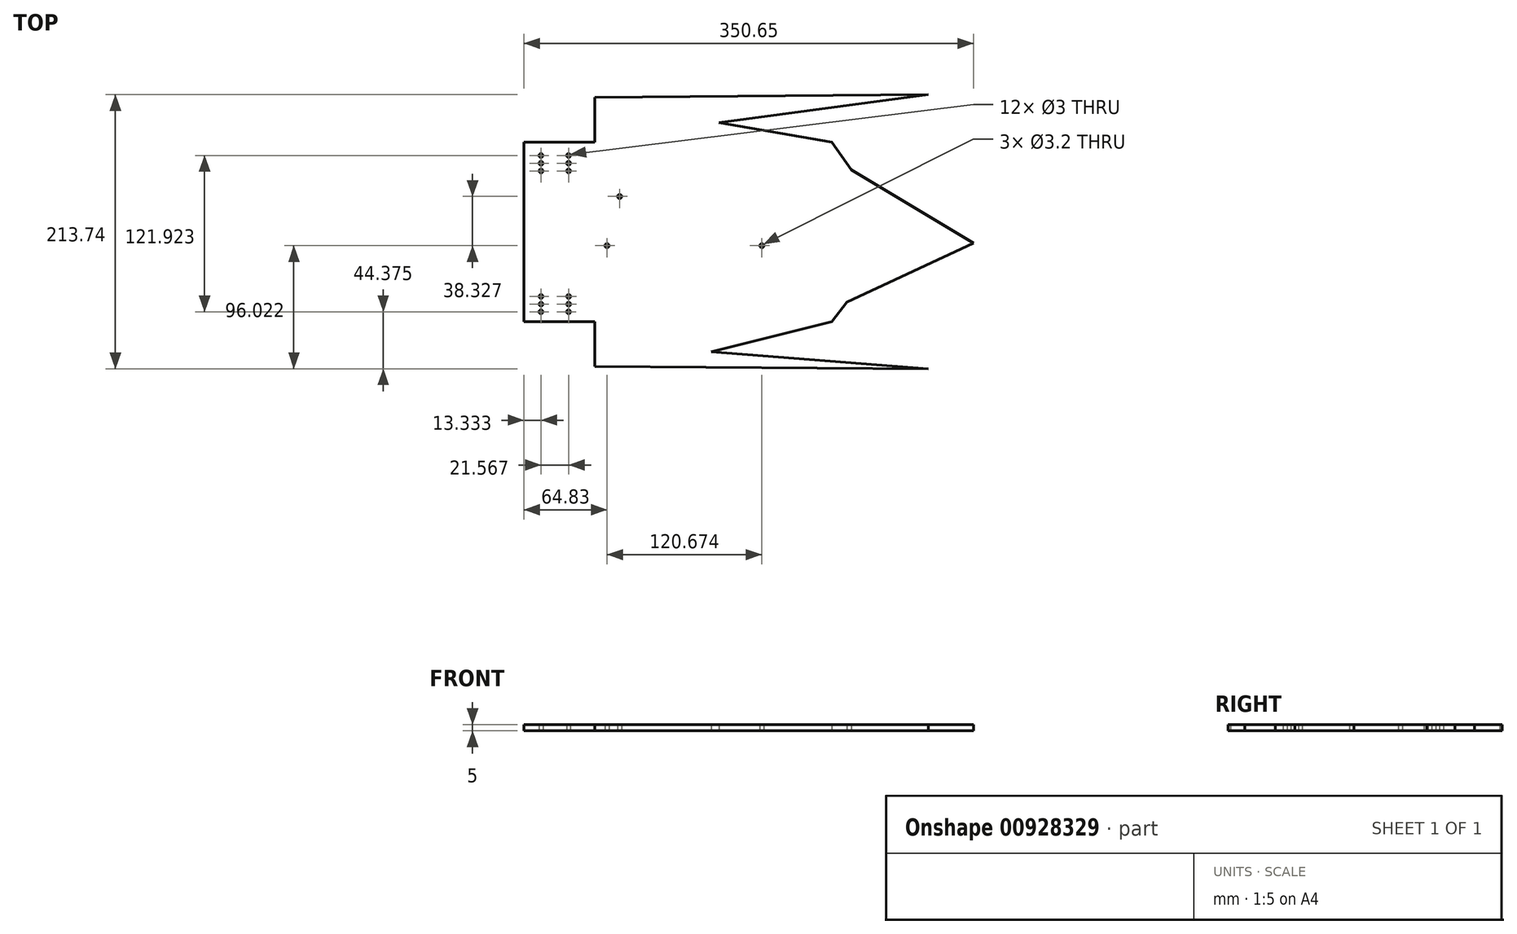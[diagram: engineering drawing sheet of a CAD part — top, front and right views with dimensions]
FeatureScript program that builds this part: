
annotation { "Feature Type Name" : "Feature", "Feature Type Description" : "" }
export const myFeature = defineFeature(function(context is Context, id is Id, definition is map)
    precondition{}
    {
        {
            var Q0;
            Q0=qCreatedBy(makeId("Top.planeOp"),FACE);
            var sketch = newSketch(context, id + "F0", { "sketchPlane" : qUnion([Q0])});
            skLineSegment(sketch, "E0.bottom", {"start": v(-128.56, -28.37) * mm, "end": v(111.44, -28.37) * mm});
            skLineSegment(sketch, "E0.top", {"start": v(-128.56, -168.37) * mm, "end": v(111.44, -168.37) * mm});
            skLineSegment(sketch, "E0.left", {"start": v(-128.56, -28.37) * mm, "end": v(-128.56, -168.37) * mm});
            skLineSegment(sketch, "E0.right", {"start": v(111.44, -28.37) * mm, "end": v(111.44, -168.37) * mm});
            skCircle(sketch, "E1", {"center": v(-115.23, -38.77) * mm, "radius": 1.5 * mm});
            skPoint(sketch, "E2.start.orphan", {"position": v(-73.23, -28.37) * mm});
            skPoint(sketch, "E3.start.orphan", {"position": v(-73.23, -168.37) * mm});
            skLineSegment(sketch, "E4", {"start": v(111.44, -28.37) * mm, "end": v(23.59, -12.98) * mm});
            skPoint(sketch, "E5.end.orphan", {"position": v(186.77, -205.07) * mm});
            skPoint(sketch, "E6", {"position": v(17.53, -28.37) * mm});
            skPoint(sketch, "E7.end.orphan", {"position": v(17.53, -191.94) * mm});
            skLineSegment(sketch, "E8", {"start": v(-73.23, -203.37) * mm, "end": v(186.77, -205.07) * mm});
            skLineSegment(sketch, "E9", {"start": v(186.77, -205.07) * mm, "end": v(17.53, -191.94) * mm});
            skPoint(sketch, "E10.start.orphan", {"position": v(186.77, 110.3) * mm});
            skLineSegment(sketch, "E11", {"start": v(186.77, 8.67) * mm, "end": v(23.59, -12.98) * mm});
            skLineSegment(sketch, "E12", {"start": v(-73.23, 6.63) * mm, "end": v(186.77, 8.67) * mm});
            skLineSegment(sketch, "E13", {"start": v(17.53, -191.94) * mm, "end": v(111.44, -168.37) * mm});
            skPoint(sketch, "E14", {"position": v(111.44, -98.37) * mm});
            skLineSegment(sketch, "E15", {"start": v(111.44, -28.37) * mm, "end": v(163.17, -102.02) * mm});
            skLineSegment(sketch, "E16", {"start": v(163.17, -102.02) * mm, "end": v(111.44, -168.37) * mm});
            skLineSegment(sketch, "E17", {"start": v(123.3, -153.15) * mm, "end": v(222.1, -107) * mm});
            skLineSegment(sketch, "E18", {"start": v(222.1, -107) * mm, "end": v(126.68, -50.07) * mm});
            skPoint(sketch, "E19.orphan", {"position": v(-73.23, -38.77) * mm});
            skPoint(sketch, "E20.end.orphan", {"position": v(-73.23, 89.23) * mm});
            skCircle(sketch, "E21.0.1.0", {"center": v(-115.2, -44.77) * mm, "radius": 1.5 * mm});
            skCircle(sketch, "E21.0.2.0", {"center": v(-115.16, -50.77) * mm, "radius": 1.5 * mm});
            skCircle(sketch, "E21.1.0.0", {"center": v(-93.73, -38.77) * mm, "radius": 1.5 * mm});
            skCircle(sketch, "E21.1.1.0", {"center": v(-93.7, -44.77) * mm, "radius": 1.5 * mm});
            skCircle(sketch, "E21.1.2.0", {"center": v(-93.66, -50.77) * mm, "radius": 1.5 * mm});
            skLineSegment(sketch, "E21.direction1", {"start": v(-115.23, -38.77) * mm, "end": v(-93.73, -38.77) * mm, "construction": true});
            skLineSegment(sketch, "E21.direction2", {"start": v(-115.23, -38.77) * mm, "end": v(-115.2, -44.77) * mm, "construction": true});
            skLineSegment(sketch, "E22", {"start": v(-145.17, -99.73) * mm, "end": v(-79.3, -99.73) * mm});
            skCircle(sketch, "E23.MirrorC", {"center": v(-115.23, -160.7) * mm, "radius": 1.5 * mm});
            skCircle(sketch, "E24.MirrorC", {"center": v(-115.2, -154.7) * mm, "radius": 1.5 * mm});
            skCircle(sketch, "E25.MirrorC", {"center": v(-93.73, -160.7) * mm, "radius": 1.5 * mm});
            skCircle(sketch, "E26.MirrorC", {"center": v(-93.66, -148.7) * mm, "radius": 1.5 * mm});
            skCircle(sketch, "E27.MirrorC", {"center": v(-93.7, -154.7) * mm, "radius": 1.5 * mm});
            skCircle(sketch, "E28.MirrorC", {"center": v(-115.16, -148.7) * mm, "radius": 1.5 * mm});
            skLineSegment(sketch, "E29.MirrorCS", {"start": v(-115.23, -160.7) * mm, "end": v(-93.73, -160.7) * mm, "construction": true});
            skLineSegment(sketch, "E30.MirrorCS", {"start": v(-115.23, -160.7) * mm, "end": v(-115.2, -154.7) * mm, "construction": true});
            skLineSegment(sketch, "E31", {"start": v(-73.23, -203.37) * mm, "end": v(-73.23, -168.37) * mm});
            skLineSegment(sketch, "E32", {"start": v(-73.23, -28.37) * mm, "end": v(-73.23, 6.63) * mm});
            skCircle(sketch, "E33", {"center": v(-63.73, -109.05) * mm, "radius": 1.6 * mm});
            skCircle(sketch, "E34", {"center": v(56.94, -109.05) * mm, "radius": 1.6 * mm});
            skLineSegment(sketch, "E35", {"start": v(127.31, 248.47) * mm, "end": v(143.1, 236.19) * mm});
            skCircle(sketch, "E36", {"center": v(16.52, 236.19) * mm, "radius": 1.6 * mm});
            skCircle(sketch, "E37", {"center": v(139.1, 236.19) * mm, "radius": 1.6 * mm});
            skCircle(sketch, "E38", {"center": v(-53.91, -70.72) * mm, "radius": 1.6 * mm});
            skPoint(sketch, "E39.end.orphan", {"position": v(127.31, 223.9) * mm});
            skPoint(sketch, "E40.end.orphan", {"position": v(125.96, 193.94) * mm});
            skCircle(sketch, "E41", {"center": v(7.57, 160.35) * mm, "radius": 15 * mm});
            skLineSegment(sketch, "E42", {"start": v(-58.33, 202.6) * mm, "end": v(-42.54, 214.87) * mm});
            skLineSegment(sketch, "E43", {"start": v(-42.54, 214.87) * mm, "end": v(56.46, 214.87) * mm});
            skLineSegment(sketch, "E44", {"start": v(56.46, 214.87) * mm, "end": v(72.25, 202.6) * mm});
            skLineSegment(sketch, "E45", {"start": v(72.25, 202.6) * mm, "end": v(56.46, 190.32) * mm});
            skLineSegment(sketch, "E46", {"start": v(56.46, 190.32) * mm, "end": v(-42.54, 190.32) * mm});
            skLineSegment(sketch, "E47", {"start": v(-42.54, 190.32) * mm, "end": v(-58.33, 202.6) * mm});
            skLineSegment(sketch, "E48", {"start": v(-42.54, 214.87) * mm, "end": v(-42.54, 190.32) * mm});
            skLineSegment(sketch, "E49", {"start": v(56.46, 214.87) * mm, "end": v(56.46, 190.32) * mm});
            skCircle(sketch, "E50", {"center": v(-54.33, 202.6) * mm, "radius": 1.6 * mm});
            skCircle(sketch, "E51", {"center": v(68.25, 202.6) * mm, "radius": 1.6 * mm});
            skLineSegment(sketch, "E52", {"start": v(7.57, 160.35) * mm, "end": v(55.11, 160.35) * mm});
            skSolve(sketch);
        }
        {
            var Q0;
            {var subQ0=sQuery(id+"F0.wireOp",EDGE,"E0.right");Q0=makeQuery(id+"F0.imprint","IMPRINT",FACE,{"disambiguationData":[TD([[makeQuery(id+"F0.imprint","IMPRINT",EDGE,{"derivedFrom":subQ0}),-1.0]])]});}
            var Q1;
            Q1=makeQuery(id+"F0.imprint","IMPRINT",FACE,{"disambiguationData":[TD([[makeQuery(id+"F0.imprint","IMPRINT",EDGE,{"derivedFrom":sQuery(id+"F0.wireOp",EDGE,"E8")}),1.0]])]});
            var Q2;
            {var subQ4=sQuery(id+"F0.wireOp",EDGE,"E17");Q2=makeQuery(id+"F0.imprint","IMPRINT",FACE,{"disambiguationData":[TD([[makeQuery(id+"F0.imprint","IMPRINT",EDGE,{"derivedFrom":subQ4}),1.0]])]});}
            var Q3;
            {var subQ4=sQuery(id+"F0.wireOp",EDGE,"E0.right");Q3=makeQuery(id+"F0.imprint","IMPRINT",FACE,{"disambiguationData":[TD([[makeQuery(id+"F0.imprint","IMPRINT",EDGE,{"derivedFrom":subQ4}),1.0]])]});}
            var Q4;
            {var subQ0=sQuery(id+"F0.wireOp",EDGE,"E4");Q4=makeQuery(id+"F0.imprint","IMPRINT",FACE,{"disambiguationData":[TD([[makeQuery(id+"F0.imprint","IMPRINT",EDGE,{"derivedFrom":subQ0}),1.0]])]});}
            extrude(context, id + "F1", {"entities" : qUnion([Q0, Q1, Q2, Q3, Q4]), "depth" : 5 * mm, "offsetDistance" : 25 * mm});
        }
    });
